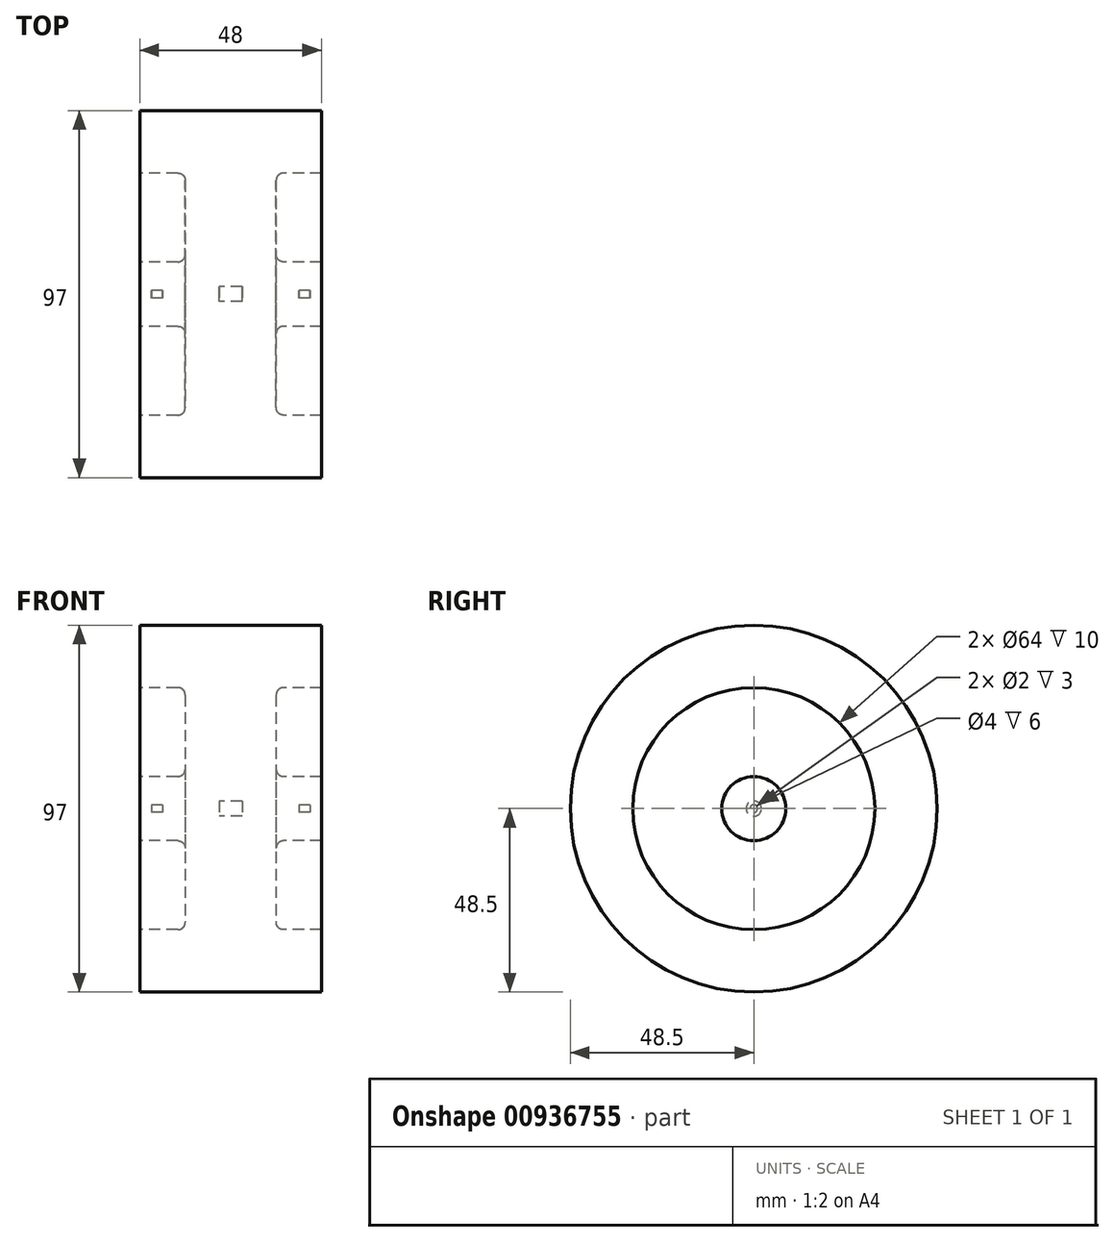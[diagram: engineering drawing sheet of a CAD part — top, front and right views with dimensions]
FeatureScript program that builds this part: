
annotation { "Feature Type Name" : "Feature", "Feature Type Description" : "" }
export const myFeature = defineFeature(function(context is Context, id is Id, definition is map)
    precondition{}
    {
        {
            var Q0;
            Q0=qCreatedBy(makeId("Front.planeOp"),FACE);
            var sketch = newSketch(context, id + "F0", { "sketchPlane" : qUnion([Q0])});
            skPoint(sketch, "E0.orphan", {"position": v(-31.57, 0) * mm});
            skPoint(sketch, "E1.start.orphan", {"position": v(24.31, 0) * mm});
            skLineSegment(sketch, "E2", {"start": v(-3, 30) * mm, "end": v(0, 30) * mm});
            skLineSegment(sketch, "E3", {"start": v(-3, 30) * mm, "end": v(-3, 32) * mm});
            skLineSegment(sketch, "E4", {"start": v(-3, 32) * mm, "end": v(-18, 32) * mm});
            skLineSegment(sketch, "E5", {"start": v(-18, 32) * mm, "end": v(-18, 33) * mm});
            skLineSegment(sketch, "E6", {"start": v(-18, 33) * mm, "end": v(-21, 33) * mm});
            skLineSegment(sketch, "E7", {"start": v(-21, 33) * mm, "end": v(-21, 32) * mm});
            skLineSegment(sketch, "E8", {"start": v(-21, 32) * mm, "end": v(-24, 32) * mm});
            skLineSegment(sketch, "E9", {"start": v(-24, 32) * mm, "end": v(-24, 40.5) * mm});
            skLineSegment(sketch, "E10", {"start": v(-24, 40.5) * mm, "end": v(-14, 40.5) * mm});
            skLineSegment(sketch, "E11", {"start": v(-12, 42.5) * mm, "end": v(-12, 62) * mm});
            skLineSegment(sketch, "E12", {"start": v(-14, 64) * mm, "end": v(-24, 64) * mm});
            skLineSegment(sketch, "E13", {"start": v(-24, 64) * mm, "end": v(-24, 80.5) * mm});
            skLineSegment(sketch, "E14", {"start": v(-24, 80.5) * mm, "end": v(0, 80.5) * mm});
            skPoint(sketch, "E15.visualSharp", {"position": v(-12, 40.5) * mm});
            skArc(sketch, "E15.filletArc", {"start": v(-14, 40.5) * mm, "mid": v(-12.59, 41.09) * mm, "end": v(-12, 42.5) * mm});
            skPoint(sketch, "E16.visualSharp", {"position": v(-12, 64) * mm});
            skArc(sketch, "E16.filletArc", {"start": v(-12, 62) * mm, "mid": v(-12.59, 63.41) * mm, "end": v(-14, 64) * mm});
            skLineSegment(sketch, "E17.MirrorCS", {"start": v(24, 80.5) * mm, "end": v(0, 80.5) * mm});
            skLineSegment(sketch, "E18.MirrorCS", {"start": v(24, 64) * mm, "end": v(24, 80.5) * mm});
            skLineSegment(sketch, "E19.MirrorCS", {"start": v(14, 64) * mm, "end": v(24, 64) * mm});
            skLineSegment(sketch, "E20.MirrorCS", {"start": v(12, 42.5) * mm, "end": v(12, 62) * mm});
            skArc(sketch, "E21.MirrorCS", {"start": v(12, 62) * mm, "mid": v(12.59, 63.41) * mm, "end": v(14, 64) * mm});
            skLineSegment(sketch, "E22.MirrorCS", {"start": v(24, 40.5) * mm, "end": v(14, 40.5) * mm});
            skArc(sketch, "E23.MirrorCS", {"start": v(14, 40.5) * mm, "mid": v(12.59, 41.09) * mm, "end": v(12, 42.5) * mm});
            skLineSegment(sketch, "E24.MirrorCS", {"start": v(24, 32) * mm, "end": v(24, 40.5) * mm});
            skLineSegment(sketch, "E25.MirrorCS", {"start": v(21, 32) * mm, "end": v(24, 32) * mm});
            skLineSegment(sketch, "E26.MirrorCS", {"start": v(21, 33) * mm, "end": v(21, 32) * mm});
            skLineSegment(sketch, "E27.MirrorCS", {"start": v(18, 33) * mm, "end": v(21, 33) * mm});
            skLineSegment(sketch, "E28.MirrorCS", {"start": v(18, 32) * mm, "end": v(18, 33) * mm});
            skLineSegment(sketch, "E29.MirrorCS", {"start": v(3, 32) * mm, "end": v(18, 32) * mm});
            skLineSegment(sketch, "E30.MirrorCS", {"start": v(3, 30) * mm, "end": v(3, 32) * mm});
            skLineSegment(sketch, "E31.MirrorCS", {"start": v(3, 30) * mm, "end": v(0, 30) * mm});
            skSolve(sketch);
        }
        {
            var Q0;
            Q0=makeQuery(id+"F0.imprint","IMPRINT",FACE,{"disambiguationData":[TD([[makeQuery(id+"F0.imprint","IMPRINT",EDGE,{"derivedFrom":sQuery(id+"F0.wireOp",EDGE,"E2")}),1.0]])]});
            var Q1;
            Q1=sQuery(id+"F0.wireOp",EDGE,"E29.MirrorCS");
            revolve(context, id + "F1", {"surfaceOperationType" : NewSurfaceOperationType.NEW, "entities" : qUnion([Q0]), "axis" : qUnion([Q1]), "revolveType" : RevolveType.FULL});
        }
    });
